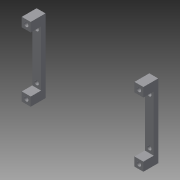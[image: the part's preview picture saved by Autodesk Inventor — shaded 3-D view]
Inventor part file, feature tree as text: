
AUTODESK INVENTOR PART (.ipt)
format: ipt  version: 2015 (Build 190159000, 159)  size: 132,608 bytes
history: native  units: in
note: dims shown in document units (in); Inventor stores cm internally (conversion verified against a paired STEP export)
features: sketch x2, extrude x2, plane x1
ambient origin geometry x8: Origin, YZ Plane, XZ Plane, XY Plane, X Axis, Y Axis, Z Axis, Center Point
bodies: Body1 (feature_tree)
feature tree (5):
  sketch  "Sketch1"  dims[d9=0.7381in d10=0.8563in]
  plane  "Work Plane1"
  extrude  "Extrusion3"  Depth=0.8563in
  extrude  "Extrusion4"  Depth=0.1181in TaperAngle=0.0deg
  sketch  "Sketch4"  dims[d11=0.1181in d12=0.1181in d13=0.0in d18=0.3937in d19=0.0in]
